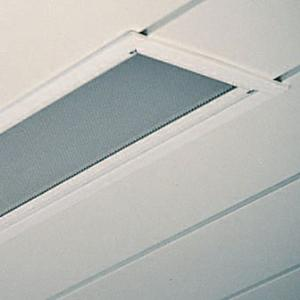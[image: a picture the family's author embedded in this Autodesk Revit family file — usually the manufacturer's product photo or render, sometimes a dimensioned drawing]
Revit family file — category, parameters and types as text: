
# Revit family: 3f_filippi_-_l_560_sp_3f_filippi_-_270959_-_l_561x24w_led_sp_221x1256
name_source: partatom
category: Lighting Fixtures
units: mm (PartAtom-declared; Revit-internal decimal feet)

## family parameters
Cut with Voids When Loaded = No
Host = Face
Light Source = No
Part Type = Normal
Room Calculation Point = No
Round Connector Dimension = Use Diameter
Shared = No

## types (1)
- 3F Filippi - L 560 SP (1 x LED, 2935 lm, 27 W, 4000 K)
    Apparent Load = 27 VA
    Approval mark = ENEC
    CIE Flux Codes = 64 90 98 100 100
    Color Rendering = 80
    Color Temperature = 4000 K
    Control Gear = Electronic ballast
    Default Elevation = 1800 mm
    Description = ILLUMINOTECHNICAL
Luminous efficiency 100% (DLOR 100%, ULOR 0%).
Initial luminous flux of the luminaire 2935 lm.
Direct symmetric distribution.
Installation Interdistance Transv.D = 1.08 x hu - Long.D = 1.18 x hu.
Tabular UGR (CIE 117 - 4H-8H; S=0.25H; 70/50/20): RUG 17.3 - 19.7.
Beam angle: 70° - 94°.
Luminous efficacy 109 lm/W.
Lifetime (L93/B10): 30000 h. (tq+25°C)
Lifetime (L90/B10): 50000 h. (tq+25°C)
Lifetime (L85/B10): 80000 h. (tq+25°C)
Lifetime (L80/B10): 100000 h. (tq+25°C)
Sudden decreased luminous flux after 50000 hours: 0% (C0).
Photobiological safety in compliance with IEC/TR 62778: RG0 risk exempt, (IEC 62471).
In compliance with IEC/EN 62722-2-1 - IEC/EN 62717 standards.

SOURCE
Linear LED module 24W/840.
Energy efficiency class (UE 2019/2020 - UE 2019/2015): D.
CIE 13.3 Colour rendering index: CRI >80 (R9 <50%).
IES TM-30 Fidelity Index: Rf = 84 Rg = 95.
CCT nominal colour temperature 4000 K.
Colour initial tolerance (MacAdam): SDCM 3.

MECHANICAL
Housing in galvannealed steel, painted in white epoxy-polyester.
SP transparent methacrylate (PMMA) flat diffuser, externally multilenticular, anti-glare, injection moulded, locked to the white painted aluminium perimetrical frame, hinged opening.
Luminaire with limited surface temperature. - D - (EN 60598-2-24)
Dimensions: 1256x221 mm, height 95 mm. Weight 5.025 kg.
IP54 protection degree for exposed part, IP20 for recessed part.
Mechanical strength to impacts IK06 (1 joule).
Glow-wire test resistance 650°C.

ELECTRICAL
Halogen Free electronic wiring 230V-50/60Hz, power factor 0.90, THD <25%, constant output current, SELV, class I, 1 driver.
Power of the luminaire 27 W.
CE - IEC 60598-1 - EN 60598-1.
SAFE FLICKER: PstLM=<1 and SVM=<0.4 (IEC TR 61547-1 and IEC TR 63158), to ensure a more comfortable and safe light.
Luminaire compliant with EN 60598-2-22 for power supply from a centralised emergency system CPSS (Central Power Supply System), not incorporated in the luminaire - high risk areas excluded. The default power and flux are 100% in AC and 100% in DC.
Ambient temperature from 0°C to +25°C.
Temperature class T6 max 85°C.
Relative humidity UR: <85%.

INSTALLATION
Pull-up recessed fitting / Slat ceiling recessed fitting.
False ceiling carving: 190x1230 mm.
All accessories dedicated to this product are available on the Catalog and on our website www.3F-Filippi.com.

APPLICATIONS
Suitable product for food production plants (HACCP), IFS (Food Version 6), BRC (GSFS Food Version 7).
Recessed installation in environments requiring protection, good visual comfort with lamp shielding and simplified cleaning.

WARNING
Luminaire designed for disposal/recycling at end-of-life.
Replaceable (LED only) light source by a professional. Replaceable control gear by a professional.
    Height = 0 mm  [stored 0 ft]
    Lamp = 1 x LED
    Lamp Light Flux = 2935 lm
    Lamp Power = 27 W
    Lamp count = 1
    Length = 1256 mm
    Lifetime = 50000 h
    Luminous efficacy = 109 lm/W
    Manufacturer = 3F Filippi
    ModVariant = No
    Model = 3F Filippi - 270959 - L 561x24W LED SP 221x1256
    Mounting Place = Ceiling
    Mounting Type = Recessed
    Number of Poles = 1
    OnlyDefault = Yes
    Power Factor = 1
    Product Name = 3F Filippi - L 560 SP
    Product group = recessed luminaire
    ProductGroupID = 4
    Protection Class = Protection class I
    Protection Degree = IP 20
    RLX_Detail_Level = 1
    RLX_Emergency_Light_Flux = 0 lm
    RLX_Emergency_Type = 0
    RLX_Emergency_Type_DB = No
    RlxData = <blob elided: 84297 chars, md5=505f30c8>
    Socket = socket
    Standby Power = 0 W
    System Light Flux = 2935 lm
    System Power = 27 W
    Type Comments = Product without accessories
    Type Image = 3ffilippi_270959.jpg
    URL = http://relux.com
    VarID = ---
    Voltage = 0 V
    Weight = 0.00 kg
    Width = 221 mm

note: [stored X ft] marks values corroborated as IEEE doubles in the binary element streams (Revit-internal decimal feet)

## geometry (parser evidence)
native form markers: Blend x4, Sweep x11
no freeform markers — native parametric forms only
